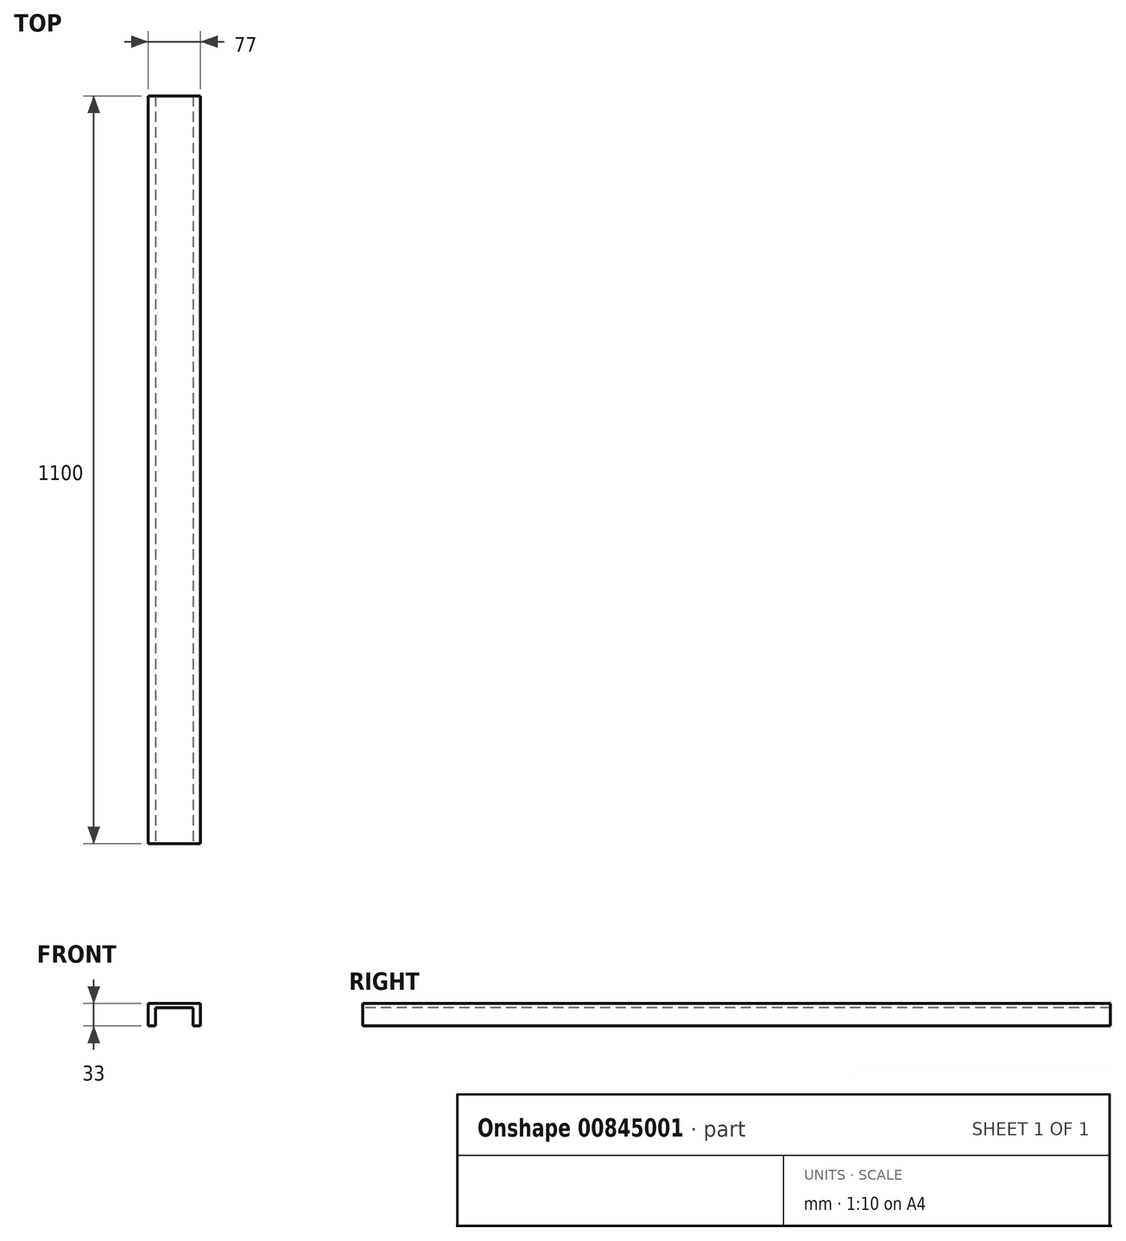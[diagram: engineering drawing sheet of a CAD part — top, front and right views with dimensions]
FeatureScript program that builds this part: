
annotation { "Feature Type Name" : "Feature", "Feature Type Description" : "" }
export const myFeature = defineFeature(function(context is Context, id is Id, definition is map)
    precondition{}
    {
        {
            var Q0;
            Q0=qCreatedBy(makeId("Front.planeOp"),FACE);
            var sketch = newSketch(context, id + "F0", { "sketchPlane" : qUnion([Q0])});
            skLineSegment(sketch, "E0", {"start": v(0, 0) * mm, "end": v(0, 33) * mm});
            skLineSegment(sketch, "E1", {"start": v(0, 33) * mm, "end": v(77, 33) * mm});
            skLineSegment(sketch, "E2", {"start": v(77, 33) * mm, "end": v(77, 0) * mm});
            skLineSegment(sketch, "E3", {"start": v(77, 0) * mm, "end": v(66, 0) * mm});
            skLineSegment(sketch, "E4", {"start": v(66, 0) * mm, "end": v(66, 26.69) * mm});
            skLineSegment(sketch, "E5", {"start": v(66, 26.69) * mm, "end": v(11, 26.69) * mm});
            skLineSegment(sketch, "E6", {"start": v(11, 26.69) * mm, "end": v(11, 0) * mm});
            skLineSegment(sketch, "E7", {"start": v(11, 0) * mm, "end": v(0, 0) * mm});
            skLineSegment(sketch, "E8.0.1.0", {"start": v(11, 40) * mm, "end": v(0, 40) * mm});
            skLineSegment(sketch, "E8.0.1.1", {"start": v(0, 40) * mm, "end": v(0, 73) * mm});
            skLineSegment(sketch, "E8.0.1.2", {"start": v(11, 66.69) * mm, "end": v(11, 40) * mm});
            skLineSegment(sketch, "E8.0.1.3", {"start": v(66, 66.69) * mm, "end": v(11, 66.69) * mm});
            skLineSegment(sketch, "E8.0.1.4", {"start": v(0, 73) * mm, "end": v(77, 73) * mm});
            skLineSegment(sketch, "E8.0.1.5", {"start": v(66, 40) * mm, "end": v(66, 66.69) * mm});
            skLineSegment(sketch, "E8.0.1.6", {"start": v(77, 73) * mm, "end": v(77, 40) * mm});
            skLineSegment(sketch, "E8.0.1.7", {"start": v(77, 40) * mm, "end": v(66, 40) * mm});
            skLineSegment(sketch, "E8.0.2.0", {"start": v(11, 80) * mm, "end": v(0, 80) * mm});
            skLineSegment(sketch, "E8.0.2.1", {"start": v(0, 80) * mm, "end": v(0, 113) * mm});
            skLineSegment(sketch, "E8.0.2.2", {"start": v(11, 106.69) * mm, "end": v(11, 80) * mm});
            skLineSegment(sketch, "E8.0.2.3", {"start": v(66, 106.69) * mm, "end": v(11, 106.69) * mm});
            skLineSegment(sketch, "E8.0.2.4", {"start": v(0, 113) * mm, "end": v(77, 113) * mm});
            skLineSegment(sketch, "E8.0.2.5", {"start": v(66, 80) * mm, "end": v(66, 106.69) * mm});
            skLineSegment(sketch, "E8.0.2.6", {"start": v(77, 113) * mm, "end": v(77, 80) * mm});
            skLineSegment(sketch, "E8.0.2.7", {"start": v(77, 80) * mm, "end": v(66, 80) * mm});
            skLineSegment(sketch, "E8.0.3.0", {"start": v(11, 120) * mm, "end": v(0, 120) * mm});
            skLineSegment(sketch, "E8.0.3.1", {"start": v(0, 120) * mm, "end": v(0, 153) * mm});
            skLineSegment(sketch, "E8.0.3.2", {"start": v(11, 146.69) * mm, "end": v(11, 120) * mm});
            skLineSegment(sketch, "E8.0.3.3", {"start": v(66, 146.69) * mm, "end": v(11, 146.69) * mm});
            skLineSegment(sketch, "E8.0.3.4", {"start": v(0, 153) * mm, "end": v(77, 153) * mm});
            skLineSegment(sketch, "E8.0.3.5", {"start": v(66, 120) * mm, "end": v(66, 146.69) * mm});
            skLineSegment(sketch, "E8.0.3.6", {"start": v(77, 153) * mm, "end": v(77, 120) * mm});
            skLineSegment(sketch, "E8.0.3.7", {"start": v(77, 120) * mm, "end": v(66, 120) * mm});
            skLineSegment(sketch, "E8.0.4.0", {"start": v(11, 160) * mm, "end": v(0, 160) * mm});
            skLineSegment(sketch, "E8.0.4.1", {"start": v(0, 160) * mm, "end": v(0, 193) * mm});
            skLineSegment(sketch, "E8.0.4.2", {"start": v(11, 186.69) * mm, "end": v(11, 160) * mm});
            skLineSegment(sketch, "E8.0.4.3", {"start": v(66, 186.69) * mm, "end": v(11, 186.69) * mm});
            skLineSegment(sketch, "E8.0.4.4", {"start": v(0, 193) * mm, "end": v(77, 193) * mm});
            skLineSegment(sketch, "E8.0.4.5", {"start": v(66, 160) * mm, "end": v(66, 186.69) * mm});
            skLineSegment(sketch, "E8.0.4.6", {"start": v(77, 193) * mm, "end": v(77, 160) * mm});
            skLineSegment(sketch, "E8.0.4.7", {"start": v(77, 160) * mm, "end": v(66, 160) * mm});
            skLineSegment(sketch, "E8.0.5.0", {"start": v(11, 200) * mm, "end": v(0, 200) * mm});
            skLineSegment(sketch, "E8.0.5.1", {"start": v(0, 200) * mm, "end": v(0, 233) * mm});
            skLineSegment(sketch, "E8.0.5.2", {"start": v(11, 226.69) * mm, "end": v(11, 200) * mm});
            skLineSegment(sketch, "E8.0.5.3", {"start": v(66, 226.69) * mm, "end": v(11, 226.69) * mm});
            skLineSegment(sketch, "E8.0.5.4", {"start": v(0, 233) * mm, "end": v(77, 233) * mm});
            skLineSegment(sketch, "E8.0.5.5", {"start": v(66, 200) * mm, "end": v(66, 226.69) * mm});
            skLineSegment(sketch, "E8.0.5.6", {"start": v(77, 233) * mm, "end": v(77, 200) * mm});
            skLineSegment(sketch, "E8.0.5.7", {"start": v(77, 200) * mm, "end": v(66, 200) * mm});
            skLineSegment(sketch, "E8.0.6.0", {"start": v(11, 240) * mm, "end": v(0, 240) * mm});
            skLineSegment(sketch, "E8.0.6.1", {"start": v(0, 240) * mm, "end": v(0, 273) * mm});
            skLineSegment(sketch, "E8.0.6.2", {"start": v(11, 266.69) * mm, "end": v(11, 240) * mm});
            skLineSegment(sketch, "E8.0.6.3", {"start": v(66, 266.69) * mm, "end": v(11, 266.69) * mm});
            skLineSegment(sketch, "E8.0.6.4", {"start": v(0, 273) * mm, "end": v(77, 273) * mm});
            skLineSegment(sketch, "E8.0.6.5", {"start": v(66, 240) * mm, "end": v(66, 266.69) * mm});
            skLineSegment(sketch, "E8.0.6.6", {"start": v(77, 273) * mm, "end": v(77, 240) * mm});
            skLineSegment(sketch, "E8.0.6.7", {"start": v(77, 240) * mm, "end": v(66, 240) * mm});
            skLineSegment(sketch, "E8.0.7.0", {"start": v(11, 280) * mm, "end": v(0, 280) * mm});
            skLineSegment(sketch, "E8.0.7.1", {"start": v(0, 280) * mm, "end": v(0, 313) * mm});
            skLineSegment(sketch, "E8.0.7.2", {"start": v(11, 306.69) * mm, "end": v(11, 280) * mm});
            skLineSegment(sketch, "E8.0.7.3", {"start": v(66, 306.69) * mm, "end": v(11, 306.69) * mm});
            skLineSegment(sketch, "E8.0.7.4", {"start": v(0, 313) * mm, "end": v(77, 313) * mm});
            skLineSegment(sketch, "E8.0.7.5", {"start": v(66, 280) * mm, "end": v(66, 306.69) * mm});
            skLineSegment(sketch, "E8.0.7.6", {"start": v(77, 313) * mm, "end": v(77, 280) * mm});
            skLineSegment(sketch, "E8.0.7.7", {"start": v(77, 280) * mm, "end": v(66, 280) * mm});
            skLineSegment(sketch, "E8.0.8.0", {"start": v(11, 320) * mm, "end": v(0, 320) * mm});
            skLineSegment(sketch, "E8.0.8.1", {"start": v(0, 320) * mm, "end": v(0, 353) * mm});
            skLineSegment(sketch, "E8.0.8.2", {"start": v(11, 346.69) * mm, "end": v(11, 320) * mm});
            skLineSegment(sketch, "E8.0.8.3", {"start": v(66, 346.69) * mm, "end": v(11, 346.69) * mm});
            skLineSegment(sketch, "E8.0.8.4", {"start": v(0, 353) * mm, "end": v(77, 353) * mm});
            skLineSegment(sketch, "E8.0.8.5", {"start": v(66, 320) * mm, "end": v(66, 346.69) * mm});
            skLineSegment(sketch, "E8.0.8.6", {"start": v(77, 353) * mm, "end": v(77, 320) * mm});
            skLineSegment(sketch, "E8.0.8.7", {"start": v(77, 320) * mm, "end": v(66, 320) * mm});
            skLineSegment(sketch, "E8.0.9.0", {"start": v(11, 360) * mm, "end": v(0, 360) * mm});
            skLineSegment(sketch, "E8.0.9.1", {"start": v(0, 360) * mm, "end": v(0, 393) * mm});
            skLineSegment(sketch, "E8.0.9.2", {"start": v(11, 386.69) * mm, "end": v(11, 360) * mm});
            skLineSegment(sketch, "E8.0.9.3", {"start": v(66, 386.69) * mm, "end": v(11, 386.69) * mm});
            skLineSegment(sketch, "E8.0.9.4", {"start": v(0, 393) * mm, "end": v(77, 393) * mm});
            skLineSegment(sketch, "E8.0.9.5", {"start": v(66, 360) * mm, "end": v(66, 386.69) * mm});
            skLineSegment(sketch, "E8.0.9.6", {"start": v(77, 393) * mm, "end": v(77, 360) * mm});
            skLineSegment(sketch, "E8.0.9.7", {"start": v(77, 360) * mm, "end": v(66, 360) * mm});
            skLineSegment(sketch, "E8.direction1", {"start": v(0, 0) * mm, "end": v(25, 0) * mm, "construction": true});
            skLineSegment(sketch, "E8.direction2", {"start": v(0, 0) * mm, "end": v(0, 40) * mm, "construction": true});
            skSolve(sketch);
        }
        {
            var Q0;
            Q0=makeQuery(id+"F0.imprint","IMPRINT",FACE,{"disambiguationData":[TD([[makeQuery(id+"F0.imprint","IMPRINT",EDGE,{"derivedFrom":sQuery(id+"F0.wireOp",EDGE,"E0")}),-1.0]])]});
            extrude(context, id + "F1", {"entities" : qUnion([Q0]), "oppositeDirection" : true, "depth" : 1100 * mm, "offsetDistance" : 25 * mm});
        }
    });
